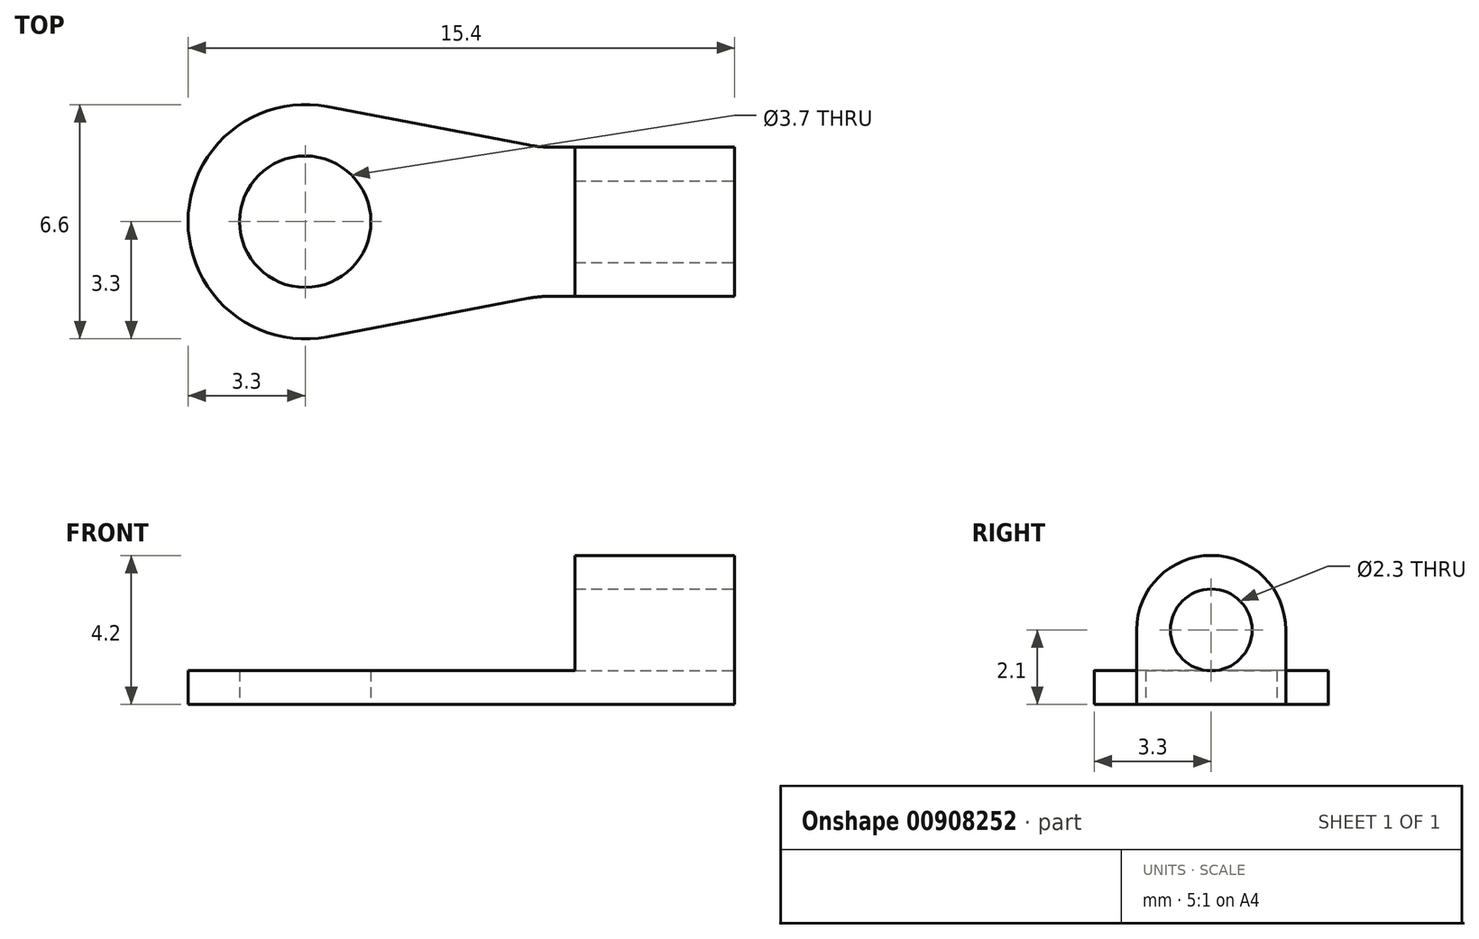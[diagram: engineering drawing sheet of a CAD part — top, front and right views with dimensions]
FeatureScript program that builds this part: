
annotation { "Feature Type Name" : "Feature", "Feature Type Description" : "" }
export const myFeature = defineFeature(function(context is Context, id is Id, definition is map)
    precondition{}
    {
        {
            var Q0;
            Q0=qCreatedBy(makeId("Top.planeOp"),FACE);
            var sketch = newSketch(context, id + "F0", { "sketchPlane" : qUnion([Q0])});
            skLineSegment(sketch, "E0.left", {"start": v(0, 3.3) * mm, "end": v(0, 3.3) * mm});
            skLineSegment(sketch, "E0.right", {"start": v(15.4, 1.2) * mm, "end": v(15.4, 5.4) * mm});
            skPoint(sketch, "E1.visualSharp", {"position": v(0, 6.6) * mm});
            skArc(sketch, "E1.filletArc", {"start": v(3.3, 6.6) * mm, "mid": v(0.97, 5.63) * mm, "end": v(0, 3.3) * mm});
            skPoint(sketch, "E2.visualSharp", {"position": v(0, 0) * mm});
            skArc(sketch, "E2.filletArc", {"start": v(0, 3.3) * mm, "mid": v(0.97, 0.97) * mm, "end": v(3.3, 0) * mm});
            skLineSegment(sketch, "E3.bottom", {"start": v(15.4, 1.2) * mm, "end": v(10.9, 1.2) * mm});
            skLineSegment(sketch, "E3.top", {"start": v(15.4, 5.4) * mm, "end": v(10.9, 5.4) * mm});
            skPoint(sketch, "E3.middle", {"position": v(15.4, 3.3) * mm});
            skLineSegment(sketch, "E4.bottom", {"start": v(10.9, 5.4) * mm, "end": v(10.21, 5.4) * mm});
            skLineSegment(sketch, "E4.top", {"start": v(10.9, 1.2) * mm, "end": v(10.21, 1.2) * mm});
            skArc(sketch, "E5", {"start": v(3.92, 6.54) * mm, "mid": v(0, 3.3) * mm, "end": v(3.92, 0.06) * mm});
            skCircle(sketch, "E6", {"center": v(3.3, 3.3) * mm, "radius": 1.85 * mm});
            skLineSegment(sketch, "E7", {"start": v(9.6, 5.46) * mm, "end": v(3.92, 6.54) * mm});
            skLineSegment(sketch, "E8", {"start": v(9.6, 1.14) * mm, "end": v(3.92, 0.06) * mm});
            skPoint(sketch, "E9.visualSharp", {"position": v(9.9, 5.4) * mm});
            skArc(sketch, "E9.filletArc", {"start": v(9.6, 5.46) * mm, "mid": v(9.9, 5.41) * mm, "end": v(10.21, 5.4) * mm});
            skPoint(sketch, "E10.visualSharp", {"position": v(9.9, 1.2) * mm});
            skArc(sketch, "E10.filletArc", {"start": v(10.21, 1.2) * mm, "mid": v(9.9, 1.19) * mm, "end": v(9.6, 1.14) * mm});
            skPoint(sketch, "E3.left.end.orphan", {"position": v(19.9, 5.4) * mm});
            skPoint(sketch, "E11.orphan", {"position": v(19.9, 1.2) * mm});
            skPoint(sketch, "E0.top.end.orphan", {"position": v(15.4, 6.6) * mm});
            skPoint(sketch, "E0.bottom.end.orphan", {"position": v(15.4, 0) * mm});
            skSolve(sketch);
        }
        {
            var Q0;
            Q0=makeQuery(id+"F0.imprint","IMPRINT",FACE,{"disambiguationData":[TD([[makeQuery(id+"F0.imprint","IMPRINT",EDGE,{"derivedFrom":sQuery(id+"F0.wireOp",EDGE,"E0.right")}),1.0]])]});
            extrude(context, id + "F1", {"entities" : qUnion([Q0]), "depth" : 0.95 * mm, "offsetDistance" : 25 * mm});
        }
        {
            var Q0;
            Q0=makeQuery(id+"F1.opExtrude","CAP_FACE",FACE,{"disambiguationData":[OSD([sQuery(id+"F0.wireOp",EDGE,"E0.right"),sQuery(id+"F0.wireOp",EDGE,"E3.bottom"),sQuery(id+"F0.wireOp",EDGE,"E3.top"),sQuery(id+"F0.wireOp",EDGE,"E4.bottom"),sQuery(id+"F0.wireOp",EDGE,"E4.top"),sQuery(id+"F0.wireOp",EDGE,"E5"),sQuery(id+"F0.wireOp",EDGE,"E6"),sQuery(id+"F0.wireOp",EDGE,"E7"),sQuery(id+"F0.wireOp",EDGE,"E8"),sQuery(id+"F0.wireOp",EDGE,"E9.filletArc"),sQuery(id+"F0.wireOp",EDGE,"E10.filletArc")])],"isStart":false});
            var sketch = newSketch(context, id + "F2", { "sketchPlane" : qUnion([Q0])});
            skLineSegment(sketch, "E12.bottom", {"start": v(15.4, 5.4) * mm, "end": v(10.9, 5.4) * mm});
            skLineSegment(sketch, "E12.top", {"start": v(15.4, 1.2) * mm, "end": v(10.9, 1.2) * mm});
            skLineSegment(sketch, "E12.left", {"start": v(15.4, 5.4) * mm, "end": v(15.4, 1.2) * mm});
            skLineSegment(sketch, "E12.right", {"start": v(10.9, 5.4) * mm, "end": v(10.9, 1.2) * mm});
            skSolve(sketch);
        }
        {
            var Q0;
            Q0=makeQuery(id+"F2.imprint","IMPRINT",FACE,{"disambiguationData":[TD([[makeQuery(id+"F2.imprint","IMPRINT",EDGE,{"derivedFrom":sQuery(id+"F2.wireOp",EDGE,"E12.bottom")}),1.0]])]});
            extrude(context, id + "F3", {"entities" : qUnion([Q0]), "operationType" : NewBodyOperationType.ADD, "depth" : 3.25 * mm, "offsetDistance" : 25 * mm});
        }
        {
            var Q0;
            Q0=makeQuery(id+"F3.opExtrude","CAP_EDGE",EDGE,{"disambiguationData":[OSD([sQuery(id+"F2.wireOp",EDGE,"E12.bottom")])],"isStart":false});
            var Q1;
            Q1=makeQuery(id+"F3.opExtrude","CAP_EDGE",EDGE,{"disambiguationData":[OSD([sQuery(id+"F2.wireOp",EDGE,"E12.top")])],"isStart":false});
            fillet(context, id + "F4", {"entities" : qUnion([Q0, Q1]), "radius" : 2.1 * mm, "tangentPropagation" : true, "allowEdgeOverflow" : false});
        }
        {
            var Q0;
            Q0=makeQuery(id+"F3.boolean.opBoolean","MERGE",FACE,{"derivedFrom":[makeQuery(id+"F1.opExtrude","SWEPT_FACE",FACE,{"disambiguationData":[OSD([sQuery(id+"F0.wireOp",EDGE,"E0.right")])]}),makeQuery(id+"F3.opExtrude","SWEPT_FACE",FACE,{"disambiguationData":[OSD([sQuery(id+"F2.wireOp",EDGE,"E12.left")])]})]});
            var sketch = newSketch(context, id + "F5", { "sketchPlane" : qUnion([Q0])});
            skCircle(sketch, "E13", {"center": v(3.3, 2.1) * mm, "radius": 1.15 * mm});
            skSolve(sketch);
        }
        {
            var Q0;
            Q0=makeQuery(id+"F5.imprint","IMPRINT",FACE,{"disambiguationData":[TD([[makeQuery(id+"F5.imprint","IMPRINT",EDGE,{"derivedFrom":sQuery(id+"F5.wireOp",EDGE,"E13")}),1.0]])]});
            extrude(context, id + "F6", {"entities" : qUnion([Q0]), "operationType" : NewBodyOperationType.REMOVE, "oppositeDirection" : true, "depth" : 25 * mm, "offsetDistance" : 25 * mm});
        }
    });
